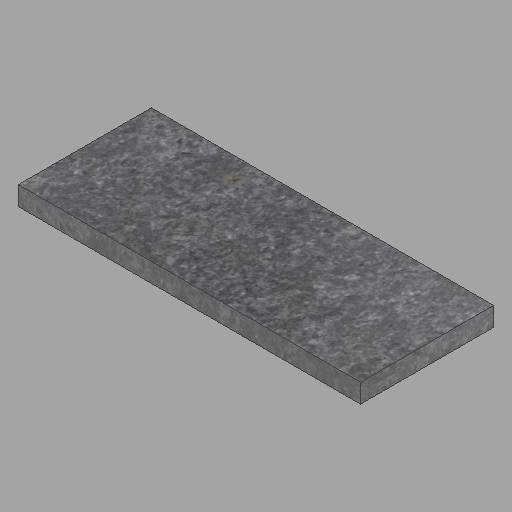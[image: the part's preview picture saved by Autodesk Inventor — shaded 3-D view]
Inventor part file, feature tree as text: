
AUTODESK INVENTOR PART (.ipt)
format: ipt  version: 2023 (Build 270158000, 158)  size: 222,208 bytes
history: native  units: in
note: dims shown in document units (in); Inventor stores cm internally (conversion verified against a paired STEP export)
features: other x1, extrude x1, sketch x1
ambient origin geometry x8: Origin, YZ Plane, XZ Plane, XY Plane, X Axis, Y Axis, Z Axis, Center Point
bodies: Solid1 (feature_tree)
feature tree (3):
  other  "2x14x36-4"
  extrude  "Extrusion1"  Depth=14.0in
  sketch  "Sketch1"  dims[d0=2.0in d1=14.0in d2=36.0in d3=0.0in]
